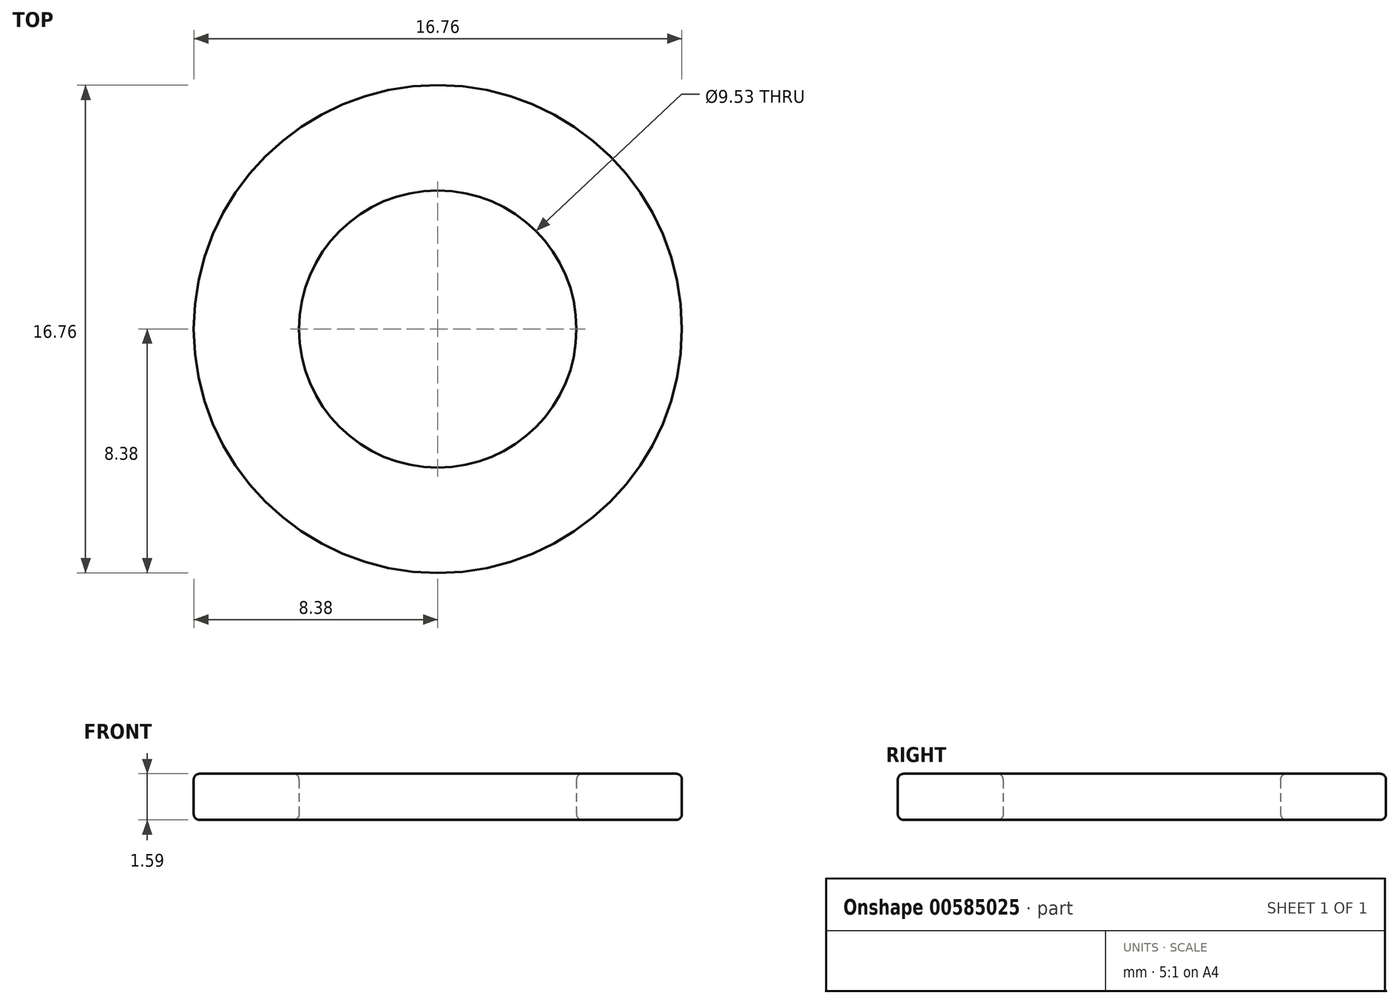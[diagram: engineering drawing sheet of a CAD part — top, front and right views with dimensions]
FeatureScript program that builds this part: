
annotation { "Feature Type Name" : "Feature", "Feature Type Description" : "" }
export const myFeature = defineFeature(function(context is Context, id is Id, definition is map)
    precondition{}
    {
        {
            var Q0;
            Q0=qCreatedBy(makeId("Top.planeOp"),FACE);
            var sketch = newSketch(context, id + "F0", { "sketchPlane" : qUnion([Q0])});
            skCircle(sketch, "E0", {"center": v(0, 0) * mm, "radius": 4.76 * mm});
            skCircle(sketch, "E1", {"center": v(0, 0) * mm, "radius": 8.38 * mm});
            skSolve(sketch);
        }
        {
            var Q0;
            Q0 = qSketchRegion(id + "F0", true);
            extrude(context, id + "F1", {"entities" : qUnion([Q0]), "depth" : 1.59 * mm, "offsetDistance" : 25.4 * mm});
        }
        {
            var Q0;
            Q0=makeQuery(id+"F1.opExtrude","CAP_EDGE",EDGE,{"disambiguationData":[OSD([sQuery(id+"F0.wireOp",EDGE,"E1")])],"isStart":true});
            var Q1;
            Q1=makeQuery(id+"F1.opExtrude","CAP_EDGE",EDGE,{"disambiguationData":[OSD([sQuery(id+"F0.wireOp",EDGE,"E1")])],"isStart":false});
            var Q2;
            Q2=makeQuery(id+"F1.opExtrude","CAP_EDGE",EDGE,{"disambiguationData":[OSD([sQuery(id+"F0.wireOp",EDGE,"E0")])],"isStart":false});
            var Q3;
            Q3=makeQuery(id+"F1.opExtrude","CAP_EDGE",EDGE,{"disambiguationData":[OSD([sQuery(id+"F0.wireOp",EDGE,"E0")])],"isStart":true});
            fillet(context, id + "F2", {"entities" : qUnion([Q0, Q1, Q2, Q3]), "radius" : 0.2 * mm, "tangentPropagation" : true, "allowEdgeOverflow" : false});
        }
    });
